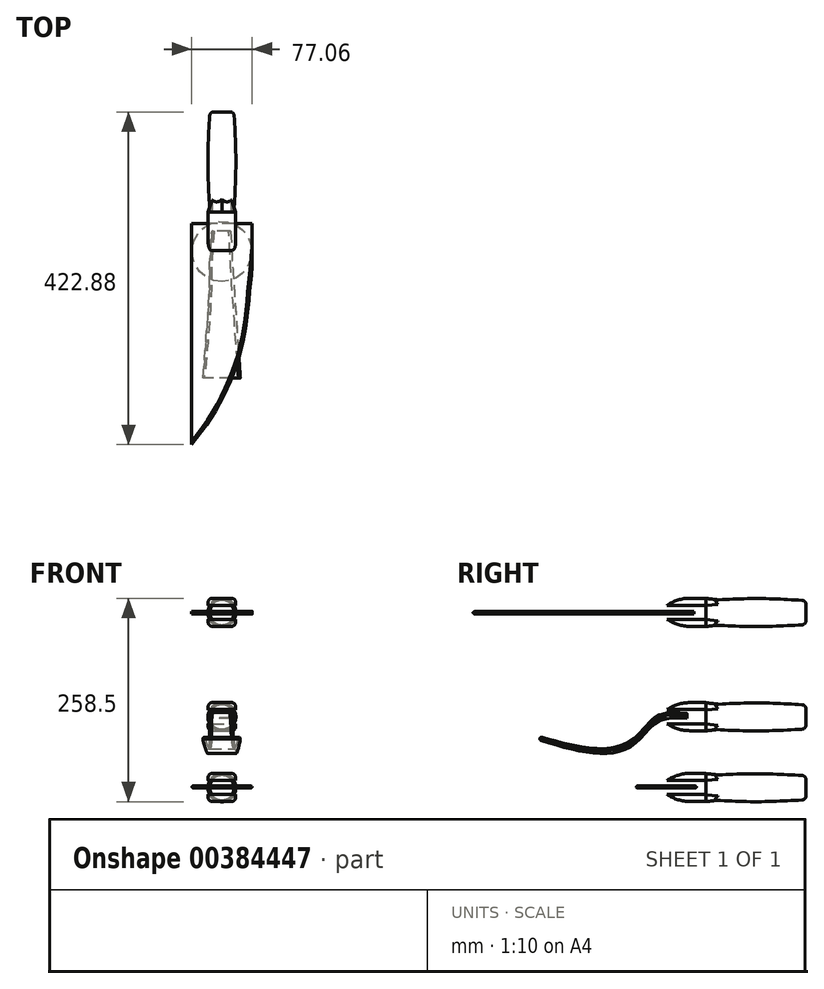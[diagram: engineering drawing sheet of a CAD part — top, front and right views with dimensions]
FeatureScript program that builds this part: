
annotation { "Feature Type Name" : "Feature", "Feature Type Description" : "" }
export const myFeature = defineFeature(function(context is Context, id is Id, definition is map)
    precondition{}
    {
        {
            var Q0;
            Q0=qCreatedBy(makeId("Front.planeOp"),FACE);
            cPlane(context, id + "F0", {"entities" : qUnion([Q0]), "cplaneType" : CPlaneType.OFFSET, "offset" : 63.5 * mm, "oppositeDirection" : true, "width" : 152.4 * mm, "height" : 152.4 * mm});
        }
        {
            var Q0;
            Q0=qCreatedBy(makeId("Front.planeOp"),FACE);
            cPlane(context, id + "F1", {"entities" : qUnion([Q0]), "cplaneType" : CPlaneType.OFFSET, "offset" : 63.5 * mm, "width" : 152.4 * mm, "height" : 152.4 * mm});
        }
        {
            var Q0;
            Q0=qCreatedBy(id+"F0.planeOp",FACE);
            var sketch = newSketch(context, id + "F2", { "sketchPlane" : qUnion([Q0])});
            skCircle(sketch, "E0", {"center": v(0, 0) * mm, "radius": 15.24 * mm});
            skSolve(sketch);
        }
        {
            var Q0;
            Q0=qCreatedBy(makeId("Front.planeOp"),FACE);
            var sketch = newSketch(context, id + "F3", { "sketchPlane" : qUnion([Q0])});
            skCircle(sketch, "E1", {"center": v(0, 0) * mm, "radius": 17.78 * mm});
            skSolve(sketch);
        }
        {
            var Q0;
            Q0=qCreatedBy(id+"F1.planeOp",FACE);
            var sketch = newSketch(context, id + "F4", { "sketchPlane" : qUnion([Q0])});
            skCircle(sketch, "E2", {"center": v(0, 0) * mm, "radius": 15.24 * mm});
            skSolve(sketch);
        }
        {
            var Q0;
            Q0=makeQuery(id+"F2.imprint","IMPRINT",FACE,{"disambiguationData":[TD([[makeQuery(id+"F2.imprint","IMPRINT",EDGE,{"derivedFrom":sQuery(id+"F2.wireOp",EDGE,"E0")}),1.0]])]});
            var Q1;
            Q1=makeQuery(id+"F3.imprint","IMPRINT",FACE,{"disambiguationData":[TD([[makeQuery(id+"F3.imprint","IMPRINT",EDGE,{"derivedFrom":sQuery(id+"F3.wireOp",EDGE,"E1")}),1.0]])]});
            var Q2;
            Q2=makeQuery(id+"F4.imprint","IMPRINT",FACE,{"disambiguationData":[TD([[makeQuery(id+"F4.imprint","IMPRINT",EDGE,{"derivedFrom":sQuery(id+"F4.wireOp",EDGE,"E2")}),1.0]])]});
            loft(context, id + "F5", {"sheetProfilesArray" : [{ "sheetProfileEntities" : qUnion([Q0]) }, { "sheetProfileEntities" : qUnion([Q1]) }, { "sheetProfileEntities" : qUnion([Q2]) }]});
        }
        {
            var Q0;
            Q0=makeQuery(id+"F5.opLoft","MID_CAP_EDGE",EDGE,{"disambiguationData":[OSD([sQuery(id+"F2.wireOp",EDGE,"E0")])],"capPos":0.0});
            fillet(context, id + "F6", {"entities" : qUnion([Q0]), "radius" : 5.08 * mm, "tangentPropagation" : true, "allowEdgeOverflow" : false});
        }
        {
            var Q0;
            Q0=qCreatedBy(id+"F1.planeOp",FACE);
            var sketch = newSketch(context, id + "F7", { "sketchPlane" : qUnion([Q0])});
            skLineSegment(sketch, "E3.bottom", {"start": v(-17.4, 18.02) * mm, "end": v(17.4, 18.02) * mm});
            skLineSegment(sketch, "E3.top", {"start": v(-17.4, 9.13) * mm, "end": v(17.4, 9.13) * mm});
            skLineSegment(sketch, "E3.left", {"start": v(-17.4, 18.02) * mm, "end": v(-17.4, 9.13) * mm});
            skLineSegment(sketch, "E3.right", {"start": v(17.4, 18.02) * mm, "end": v(17.4, 9.13) * mm});
            skPoint(sketch, "E3.middle", {"position": v(0, 13.57) * mm});
            skLineSegment(sketch, "E4.bottom", {"start": v(-17.4, -17.73) * mm, "end": v(17.4, -17.73) * mm});
            skLineSegment(sketch, "E4.top", {"start": v(-17.4, -8.84) * mm, "end": v(17.4, -8.84) * mm});
            skLineSegment(sketch, "E4.left", {"start": v(-17.4, -17.73) * mm, "end": v(-17.4, -8.84) * mm});
            skLineSegment(sketch, "E4.right", {"start": v(17.4, -17.73) * mm, "end": v(17.4, -8.84) * mm});
            skPoint(sketch, "E4.middle", {"position": v(0, -13.29) * mm});
            skSolve(sketch);
        }
        {
            var Q0;
            Q0=qCreatedBy(makeId("Front.planeOp"),FACE);
            cPlane(context, id + "F8", {"entities" : qUnion([Q0]), "cplaneType" : CPlaneType.OFFSET, "offset" : 45.97 * mm, "width" : 152.4 * mm, "height" : 152.4 * mm});
        }
        {
            var Q0;
            Q0=qCreatedBy(id+"F8.planeOp",FACE);
            var sketch = newSketch(context, id + "F9", { "sketchPlane" : qUnion([Q0])});
            skLineSegment(sketch, "E5.bottom", {"start": v(-11.43, 16.43) * mm, "end": v(11.43, 16.43) * mm});
            skLineSegment(sketch, "E5.top", {"start": v(-11.43, 10.72) * mm, "end": v(11.43, 10.72) * mm});
            skLineSegment(sketch, "E5.left", {"start": v(-11.43, 16.43) * mm, "end": v(-11.43, 10.72) * mm});
            skLineSegment(sketch, "E5.right", {"start": v(11.43, 16.43) * mm, "end": v(11.43, 10.72) * mm});
            skPoint(sketch, "E5.middle", {"position": v(0, 13.57) * mm});
            skLineSegment(sketch, "E6.bottom", {"start": v(-11.43, -15.95) * mm, "end": v(11.43, -15.95) * mm});
            skLineSegment(sketch, "E6.top", {"start": v(-11.43, -10.87) * mm, "end": v(11.43, -10.87) * mm});
            skLineSegment(sketch, "E6.left", {"start": v(-11.43, -15.95) * mm, "end": v(-11.43, -10.87) * mm});
            skLineSegment(sketch, "E6.right", {"start": v(11.43, -15.95) * mm, "end": v(11.43, -10.87) * mm});
            skPoint(sketch, "E6.middle", {"position": v(0, -13.4) * mm});
            skSolve(sketch);
        }
        {
            var Q0;
            Q0=qCreatedBy(id+"F8.planeOp",FACE);
            cPlane(context, id + "F10", {"entities" : qUnion([Q0]), "cplaneType" : CPlaneType.OFFSET, "offset" : 66.8 * mm, "width" : 152.4 * mm, "height" : 152.4 * mm});
        }
        {
            var Q0;
            Q0=qCreatedBy(id+"F10.planeOp",FACE);
            var sketch = newSketch(context, id + "F11", { "sketchPlane" : qUnion([Q0])});
            skLineSegment(sketch, "E7.bottom", {"start": v(-17.4, 18.22) * mm, "end": v(17.4, 18.22) * mm});
            skLineSegment(sketch, "E7.top", {"start": v(-17.4, 9.33) * mm, "end": v(17.4, 9.33) * mm});
            skLineSegment(sketch, "E7.left", {"start": v(-17.4, 18.22) * mm, "end": v(-17.4, 9.33) * mm});
            skLineSegment(sketch, "E7.right", {"start": v(17.4, 18.22) * mm, "end": v(17.4, 9.33) * mm});
            skPoint(sketch, "E7.middle", {"position": v(0, 13.77) * mm});
            skLineSegment(sketch, "E8.bottom", {"start": v(-17.4, -8.6) * mm, "end": v(17.4, -8.6) * mm});
            skLineSegment(sketch, "E8.top", {"start": v(-17.4, -17.49) * mm, "end": v(17.4, -17.49) * mm});
            skLineSegment(sketch, "E8.left", {"start": v(-17.4, -8.6) * mm, "end": v(-17.4, -17.49) * mm});
            skLineSegment(sketch, "E8.right", {"start": v(17.4, -8.6) * mm, "end": v(17.4, -17.49) * mm});
            skPoint(sketch, "E8.middle", {"position": v(0, -13.04) * mm});
            skSolve(sketch);
        }
        {
            var Q1;
            Q1=makeQuery(id+"F7.imprint","IMPRINT",FACE,{"disambiguationData":[TD([[makeQuery(id+"F7.imprint","IMPRINT",EDGE,{"derivedFrom":sQuery(id+"F7.wireOp",EDGE,"E3.bottom")}),-1.0]])]});
            var Q2;
            Q2=makeQuery(id+"F9.imprint","IMPRINT",FACE,{"disambiguationData":[TD([[makeQuery(id+"F9.imprint","IMPRINT",EDGE,{"derivedFrom":sQuery(id+"F9.wireOp",EDGE,"E5.bottom")}),-1.0]])]});
            loft(context, id + "F12", {"operationType" : NewBodyOperationType.ADD, "sheetProfilesArray" : [{ "sheetProfileEntities" : qUnion([Q1]) }, { "sheetProfileEntities" : qUnion([Q2]) }]});
        }
        {
            var Q1;
            Q1=makeQuery(id+"F7.imprint","IMPRINT",FACE,{"disambiguationData":[TD([[makeQuery(id+"F7.imprint","IMPRINT",EDGE,{"derivedFrom":sQuery(id+"F7.wireOp",EDGE,"E4.bottom")}),1.0]])]});
            var Q2;
            Q2=makeQuery(id+"F9.imprint","IMPRINT",FACE,{"disambiguationData":[TD([[makeQuery(id+"F9.imprint","IMPRINT",EDGE,{"derivedFrom":sQuery(id+"F9.wireOp",EDGE,"E6.bottom")}),1.0]])]});
            loft(context, id + "F13", {"operationType" : NewBodyOperationType.ADD, "sheetProfilesArray" : [{ "sheetProfileEntities" : qUnion([Q1]) }, { "sheetProfileEntities" : qUnion([Q2]) }]});
        }
        {
            var Q0;
            Q0=makeQuery(id+"F11.imprint","IMPRINT",FACE,{"disambiguationData":[TD([[makeQuery(id+"F11.imprint","IMPRINT",EDGE,{"derivedFrom":sQuery(id+"F11.wireOp",EDGE,"E7.bottom")}),-1.0]])]});
            extrude(context, id + "F14", {"entities" : qUnion([Q0]), "operationType" : NewBodyOperationType.ADD, "oppositeDirection" : true, "depth" : 49.28 * mm});
        }
        {
            var Q0;
            Q0=makeQuery(id+"F11.imprint","IMPRINT",FACE,{"disambiguationData":[TD([[makeQuery(id+"F11.imprint","IMPRINT",EDGE,{"derivedFrom":sQuery(id+"F11.wireOp",EDGE,"E8.bottom")}),-1.0]])]});
            extrude(context, id + "F15", {"entities" : qUnion([Q0]), "operationType" : NewBodyOperationType.ADD, "oppositeDirection" : true, "depth" : 49.53 * mm});
        }
        {
            var Q0;
            Q0=makeQuery(id+"F14.opExtrude","CAP_EDGE",EDGE,{"disambiguationData":[OSD([sQuery(id+"F11.wireOp",EDGE,"E7.bottom")])],"isStart":true});
            var Q1;
            Q1=makeQuery(id+"F15.opExtrude","CAP_EDGE",EDGE,{"disambiguationData":[OSD([sQuery(id+"F11.wireOp",EDGE,"E8.top")])],"isStart":true});
            fillet(context, id + "F16", {"entities" : qUnion([Q0, Q1]), "radius" : 50.8 * mm, "tangentPropagation" : true, "allowEdgeOverflow" : false});
        }
        {
            var Q0;
            Q0=makeQuery(id+"F13.opLoft","SWEPT_EDGE",EDGE,{"disambiguationData":[OSD([sQuery(id+"F7.wireOp",EDGE,"E4.bottom"),sQuery(id+"F7.wireOp",EDGE,"E4.left"),sQuery(id+"F9.wireOp",EDGE,"E6.bottom"),sQuery(id+"F9.wireOp",EDGE,"E6.left")])]});
            var Q1;
            Q1=makeQuery(id+"F13.opLoft","SWEPT_EDGE",EDGE,{"disambiguationData":[OSD([sQuery(id+"F7.wireOp",EDGE,"E4.bottom"),sQuery(id+"F7.wireOp",EDGE,"E4.right"),sQuery(id+"F9.wireOp",EDGE,"E6.bottom"),sQuery(id+"F9.wireOp",EDGE,"E6.right")])]});
            var Q2;
            Q2=makeQuery(id+"F12.opLoft","SWEPT_EDGE",EDGE,{"disambiguationData":[OSD([sQuery(id+"F7.wireOp",EDGE,"E3.bottom"),sQuery(id+"F7.wireOp",EDGE,"E3.left"),sQuery(id+"F9.wireOp",EDGE,"E5.bottom"),sQuery(id+"F9.wireOp",EDGE,"E5.left")])]});
            var Q3;
            Q3=makeQuery(id+"F12.opLoft","SWEPT_EDGE",EDGE,{"disambiguationData":[OSD([sQuery(id+"F7.wireOp",EDGE,"E3.bottom"),sQuery(id+"F7.wireOp",EDGE,"E3.right"),sQuery(id+"F9.wireOp",EDGE,"E5.bottom"),sQuery(id+"F9.wireOp",EDGE,"E5.right")])]});
            fillet(context, id + "F17", {"entities" : qUnion([Q0, Q1, Q2, Q3]), "radius" : 25.4 * mm, "tangentPropagation" : true, "allowEdgeOverflow" : false});
        }
        {
            var Q0;
            Q0=makeQuery(id+"F14.opExtrude","SWEPT_EDGE",EDGE,{"disambiguationData":[OSD([sQuery(id+"F11.wireOp",EDGE,"E7.bottom"),sQuery(id+"F11.wireOp",EDGE,"E7.right")])]});
            var Q1;
            Q1=makeQuery(id+"F14.opExtrude","SWEPT_EDGE",EDGE,{"disambiguationData":[OSD([sQuery(id+"F11.wireOp",EDGE,"E7.bottom"),sQuery(id+"F11.wireOp",EDGE,"E7.left")])]});
            var Q2;
            {var subQ3=sQuery(id+"F11.wireOp",EDGE,"E8.left");var subQ4=sQuery(id+"F11.wireOp",EDGE,"E8.top");Q2=makeQuery(id+"F15.boolean.opBoolean","SPLIT",EDGE,{"disambiguationData":[TD([makeQuery(id+"F15.opExtrude","CAP_FACE",FACE,{"disambiguationData":[OSD([sQuery(id+"F11.wireOp",EDGE,"E8.bottom"),subQ4,subQ3,sQuery(id+"F11.wireOp",EDGE,"E8.right")])],"isStart":false})])],"derivedFrom":makeQuery(id+"F15.opExtrude","SWEPT_EDGE",EDGE,{"disambiguationData":[OSD([subQ4,subQ3])]})});}
            var Q3;
            {var subQ3=sQuery(id+"F11.wireOp",EDGE,"E8.right");var subQ4=sQuery(id+"F11.wireOp",EDGE,"E8.top");Q3=makeQuery(id+"F15.boolean.opBoolean","SPLIT",EDGE,{"disambiguationData":[TD([makeQuery(id+"F15.opExtrude","CAP_FACE",FACE,{"disambiguationData":[OSD([sQuery(id+"F11.wireOp",EDGE,"E8.bottom"),subQ4,sQuery(id+"F11.wireOp",EDGE,"E8.left"),subQ3])],"isStart":false})])],"derivedFrom":makeQuery(id+"F15.opExtrude","SWEPT_EDGE",EDGE,{"disambiguationData":[OSD([subQ4,subQ3])]})});}
            fillet(context, id + "F18", {"entities" : qUnion([Q0, Q1, Q2, Q3]), "radius" : 5.08 * mm, "tangentPropagation" : true, "allowEdgeOverflow" : false});
        }
        {
            var Q0;
            Q0=qCreatedBy(makeId("Front.planeOp"),FACE);
            cPlane(context, id + "F19", {"entities" : qUnion([Q0]), "cplaneType" : CPlaneType.OFFSET, "offset" : 90.68 * mm, "width" : 152.4 * mm, "height" : 152.4 * mm});
        }
        {
            var Q0;
            Q0=qCreatedBy(id+"F19.planeOp",FACE);
            var sketch = newSketch(context, id + "F20", { "sketchPlane" : qUnion([Q0])});
            skLineSegment(sketch, "E9", {"start": v(28.47, 0) * mm, "end": v(-29.24, 0) * mm, "construction": true});
            skSolve(sketch);
        }
        {
            var Q0;
            Q0=sQuery(id+"F20.wireOp",EDGE,"E9");
            cPlane(context, id + "F21", {"entities" : qUnion([Q0]), "cplaneType" : CPlaneType.LINE_ANGLE, "offset" : 25.4 * mm, "angle" : 90 * degree, "width" : 152.4 * mm, "height" : 152.4 * mm});
        }
        {
            var Q0;
            Q0=qCreatedBy(id+"F21.planeOp",FACE);
            var sketch = newSketch(context, id + "F22", { "sketchPlane" : qUnion([Q0])});
            skCircle(sketch, "E10", {"center": v(0, -113.92) * mm, "radius": 38.1 * mm});
            skSolve(sketch);
        }
        {
            var Q0;
            Q0=makeQuery(id+"F22.imprint","IMPRINT",FACE,{"disambiguationData":[TD([[makeQuery(id+"F22.imprint","IMPRINT",EDGE,{"derivedFrom":sQuery(id+"F22.wireOp",EDGE,"E10")}),1.0]])]});
            extrude(context, id + "F23", {"entities" : qUnion([Q0]), "depth" : 2.03 * mm});
        }
        {
            var Q0;
            Q0=makeQuery(id+"F23.opExtrude","CAP_EDGE",EDGE,{"disambiguationData":[OSD([sQuery(id+"F22.wireOp",EDGE,"E10")])],"isStart":true});
            var Q1;
            Q1=makeQuery(id+"F23.opExtrude","CAP_EDGE",EDGE,{"disambiguationData":[OSD([sQuery(id+"F22.wireOp",EDGE,"E10")])],"isStart":false});
            fillet(context, id + "F24", {"entities" : qUnion([Q0, Q1]), "radius" : 1.02 * mm, "tangentPropagation" : true, "allowEdgeOverflow" : false});
        }
        {
            var Q0;
            Q0=makeQuery(id+"F5.opLoft","SWEPT_BODY",BODY,{"disambiguationData":[OSD([makeQuery(id+"F2.imprint","IMPRINT",FACE,{"disambiguationData":[TD([[makeQuery(id+"F2.imprint","IMPRINT",EDGE,{"derivedFrom":sQuery(id+"F2.wireOp",EDGE,"E0")}),1.0]])]}),sQuery(id+"F3.wireOp",EDGE,"E1"),makeQuery(id+"F4.imprint","IMPRINT",FACE,{"disambiguationData":[TD([[makeQuery(id+"F4.imprint","IMPRINT",EDGE,{"derivedFrom":sQuery(id+"F4.wireOp",EDGE,"E2")}),1.0]])]})])]});
            transform(context, id + "F25", {"entities" : qUnion([Q0]), "transformType" : TransformType.TRANSLATION_3D, "dx" : 0 * mm, "dy" : 0 * mm, "dz" : 89.92 * mm, "makeCopy" : true});
        }
        {
            var Q0;
            Q0=qCreatedBy(id+"F21.planeOp",FACE);
            cPlane(context, id + "F26", {"entities" : qUnion([Q0]), "cplaneType" : CPlaneType.OFFSET, "offset" : 91.7 * mm, "width" : 152.4 * mm, "height" : 152.4 * mm});
        }
        {
            var Q0;
            Q0=qCreatedBy(id+"F26.planeOp",FACE);
            var sketch = newSketch(context, id + "F27", { "sketchPlane" : qUnion([Q0])});
            skLineSegment(sketch, "E11", {"start": v(-24.98, -87.77) * mm, "end": v(24.86, -87.77) * mm, "construction": true});
            skSolve(sketch);
        }
        {
            var Q0;
            Q0=sQuery(id+"F27.wireOp",EDGE,"E11");
            cPlane(context, id + "F28", {"entities" : qUnion([Q0]), "cplaneType" : CPlaneType.LINE_ANGLE, "offset" : 25.4 * mm, "angle" : 0 * degree, "width" : 152.4 * mm, "height" : 152.4 * mm});
        }
        {
            var Q0;
            Q0=qCreatedBy(id+"F28.planeOp",FACE);
            var sketch = newSketch(context, id + "F29", { "sketchPlane" : qUnion([Q0])});
            skLineSegment(sketch, "E12.bottom", {"start": v(-11.27, 88.13) * mm, "end": v(12.68, 88.13) * mm});
            skLineSegment(sketch, "E12.top", {"start": v(-11.27, 94.6) * mm, "end": v(12.68, 94.6) * mm});
            skLineSegment(sketch, "E12.left", {"start": v(-11.27, 88.13) * mm, "end": v(-11.27, 94.6) * mm});
            skLineSegment(sketch, "E12.right", {"start": v(12.68, 88.13) * mm, "end": v(12.68, 94.6) * mm});
            skPoint(sketch, "E12.middle", {"position": v(0.7, 91.37) * mm});
            skSolve(sketch);
        }
        {
            var Q0;
            Q0=qCreatedBy(id+"F28.planeOp",FACE);
            cPlane(context, id + "F30", {"entities" : qUnion([Q0]), "cplaneType" : CPlaneType.OFFSET, "offset" : 37.85 * mm, "oppositeDirection" : true, "width" : 152.4 * mm, "height" : 152.4 * mm});
        }
        {
            var Q0;
            Q0=qCreatedBy(id+"F30.planeOp",FACE);
            var sketch = newSketch(context, id + "F31", { "sketchPlane" : qUnion([Q0])});
            skLineSegment(sketch, "E13.bottom", {"start": v(15.27, 90.72) * mm, "end": v(-13.2, 90.72) * mm});
            skLineSegment(sketch, "E13.top", {"start": v(15.27, 83.6) * mm, "end": v(-13.2, 83.6) * mm});
            skLineSegment(sketch, "E13.left", {"start": v(15.27, 90.72) * mm, "end": v(15.27, 83.6) * mm});
            skLineSegment(sketch, "E13.right", {"start": v(-13.2, 90.72) * mm, "end": v(-13.2, 83.6) * mm});
            skPoint(sketch, "E13.middle", {"position": v(1.03, 87.16) * mm});
            skSolve(sketch);
        }
        {
            var Q0;
            Q0=qCreatedBy(id+"F30.planeOp",FACE);
            cPlane(context, id + "F32", {"entities" : qUnion([Q0]), "cplaneType" : CPlaneType.OFFSET, "offset" : 24.9 * mm, "oppositeDirection" : true, "width" : 152.4 * mm, "height" : 152.4 * mm});
        }
        {
            var Q0;
            Q0=qCreatedBy(id+"F32.planeOp",FACE);
            var sketch = newSketch(context, id + "F33", { "sketchPlane" : qUnion([Q0])});
            skLineSegment(sketch, "E14.bottom", {"start": v(15.6, 66.13) * mm, "end": v(-14.82, 66.13) * mm});
            skLineSegment(sketch, "E14.top", {"start": v(15.6, 59) * mm, "end": v(-14.82, 59) * mm});
            skLineSegment(sketch, "E14.left", {"start": v(15.6, 66.13) * mm, "end": v(15.6, 59) * mm});
            skLineSegment(sketch, "E14.right", {"start": v(-14.82, 66.13) * mm, "end": v(-14.82, 59) * mm});
            skPoint(sketch, "E14.middle", {"position": v(0.38, 62.57) * mm});
            skSolve(sketch);
        }
        {
            var Q0;
            Q0=qCreatedBy(id+"F32.planeOp",FACE);
            cPlane(context, id + "F34", {"entities" : qUnion([Q0]), "cplaneType" : CPlaneType.OFFSET, "offset" : 124.2 * mm, "oppositeDirection" : true, "width" : 152.4 * mm, "height" : 152.4 * mm});
        }
        {
            var Q0;
            Q0=qCreatedBy(id+"F34.planeOp",FACE);
            var sketch = newSketch(context, id + "F35", { "sketchPlane" : qUnion([Q0])});
            skLineSegment(sketch, "E15.bottom", {"start": v(24.2, 60.76) * mm, "end": v(-23.4, 60.76) * mm});
            skLineSegment(sketch, "E15.top", {"start": v(24.2, 64.84) * mm, "end": v(-23.4, 64.84) * mm});
            skLineSegment(sketch, "E15.left", {"start": v(24.2, 60.76) * mm, "end": v(24.2, 64.84) * mm});
            skLineSegment(sketch, "E15.right", {"start": v(-23.4, 60.76) * mm, "end": v(-23.4, 64.84) * mm});
            skPoint(sketch, "E15.middle", {"position": v(0.4, 62.8) * mm});
            skSolve(sketch);
        }
        {
            var Q0;
            Q0=makeQuery(id+"F29.imprint","IMPRINT",FACE,{"disambiguationData":[TD([[makeQuery(id+"F29.imprint","IMPRINT",EDGE,{"derivedFrom":sQuery(id+"F29.wireOp",EDGE,"E12.bottom")}),1.0]])]});
            var Q1;
            Q1=makeQuery(id+"F31.imprint","IMPRINT",FACE,{"disambiguationData":[TD([[makeQuery(id+"F31.imprint","IMPRINT",EDGE,{"derivedFrom":sQuery(id+"F31.wireOp",EDGE,"E13.bottom")}),1.0]])]});
            var Q2;
            Q2=makeQuery(id+"F33.imprint","IMPRINT",FACE,{"disambiguationData":[TD([[makeQuery(id+"F33.imprint","IMPRINT",EDGE,{"derivedFrom":sQuery(id+"F33.wireOp",EDGE,"E14.bottom")}),1.0]])]});
            var Q3;
            Q3=makeQuery(id+"F35.imprint","IMPRINT",FACE,{"disambiguationData":[TD([[makeQuery(id+"F35.imprint","IMPRINT",EDGE,{"derivedFrom":sQuery(id+"F35.wireOp",EDGE,"E15.bottom")}),-1.0]])]});
            loft(context, id + "F36", {"sheetProfilesArray" : [{ "sheetProfileEntities" : qUnion([Q0]) }, { "sheetProfileEntities" : qUnion([Q1]) }, { "sheetProfileEntities" : qUnion([Q2]) }, { "sheetProfileEntities" : qUnion([Q3]) }]});
        }
        {
            var Q0;
            Q0=makeQuery(id+"F36.opLoft","MID_CAP_EDGE",EDGE,{"disambiguationData":[OSD([sQuery(id+"F35.wireOp",EDGE,"E15.top"),sQuery(id+"F35.wireOp",EDGE,"E15.left"),sQuery(id+"F35.wireOp",EDGE,"E15.right")])],"capPos":3.0});
            var Q1;
            Q1=makeQuery(id+"F36.opLoft","MID_CAP_EDGE",EDGE,{"disambiguationData":[OSD([sQuery(id+"F35.wireOp",EDGE,"E15.bottom"),sQuery(id+"F35.wireOp",EDGE,"E15.left"),sQuery(id+"F35.wireOp",EDGE,"E15.right")])],"capPos":3.0});
            var Q2;
            Q2=makeQuery(id+"F36.opLoft","SWEPT_EDGE",EDGE,{"disambiguationData":[OSD([sQuery(id+"F29.wireOp",EDGE,"E12.top"),sQuery(id+"F29.wireOp",EDGE,"E12.left"),sQuery(id+"F31.wireOp",EDGE,"E13.bottom"),sQuery(id+"F31.wireOp",EDGE,"E13.right")])]});
            var Q3;
            Q3=makeQuery(id+"F36.opLoft","SWEPT_EDGE",EDGE,{"disambiguationData":[OSD([sQuery(id+"F29.wireOp",EDGE,"E12.top"),sQuery(id+"F29.wireOp",EDGE,"E12.right"),sQuery(id+"F31.wireOp",EDGE,"E13.bottom"),sQuery(id+"F31.wireOp",EDGE,"E13.left")])]});
            fillet(context, id + "F37", {"entities" : qUnion([Q0, Q1, Q2, Q3]), "radius" : 2.54 * mm, "tangentPropagation" : true, "allowEdgeOverflow" : false});
        }
        {
            var Q0;
            Q0=makeQuery(id+"F25.opPattern","COPY",BODY,{"derivedFrom":makeQuery(id+"F5.opLoft","SWEPT_BODY",BODY,{"disambiguationData":[OSD([makeQuery(id+"F2.imprint","IMPRINT",FACE,{"disambiguationData":[TD([[makeQuery(id+"F2.imprint","IMPRINT",EDGE,{"derivedFrom":sQuery(id+"F2.wireOp",EDGE,"E0")}),1.0]])]}),sQuery(id+"F3.wireOp",EDGE,"E1"),makeQuery(id+"F4.imprint","IMPRINT",FACE,{"disambiguationData":[TD([[makeQuery(id+"F4.imprint","IMPRINT",EDGE,{"derivedFrom":sQuery(id+"F4.wireOp",EDGE,"E2")}),1.0]])]})])]}),"instanceName":"1"});
            transform(context, id + "F38", {"entities" : qUnion([Q0]), "transformType" : TransformType.TRANSLATION_3D, "dx" : 0 * mm, "dy" : 0 * mm, "dz" : 132.6 * mm, "makeCopy" : true});
        }
        {
            var Q0;
            Q0=qCreatedBy(id+"F26.planeOp",FACE);
            cPlane(context, id + "F39", {"entities" : qUnion([Q0]), "cplaneType" : CPlaneType.OFFSET, "offset" : 130.56 * mm, "width" : 152.4 * mm, "height" : 152.4 * mm});
        }
        {
            var Q0;
            Q0=qCreatedBy(id+"F39.planeOp",FACE);
            var sketch = newSketch(context, id + "F40", { "sketchPlane" : qUnion([Q0])});
            skLineSegment(sketch, "E16.bottom", {"start": v(38.42, -78.65) * mm, "end": v(-38.64, -78.65) * mm});
            skLineSegment(sketch, "E16.left", {"start": v(38.42, -78.65) * mm, "end": v(38.42, -134.4) * mm});
            skLineSegment(sketch, "E16.right", {"start": v(-38.64, -78.65) * mm, "end": v(-38.64, -359.57) * mm});
            skFitSpline(sketch, "E17", {"points": [v(38.42, -134.4) * mm, v(33.5, -183.59) * mm, v(23.12, -244.25) * mm, v(-9.13, -318.04) * mm, v(-38.64, -359.57) * mm], "startDerivative": vector(-20.97, -213.3) * mm, "endDerivative": vector(-127.7, -161.77) * mm});
            skSolve(sketch);
        }
        {
            var Q0;
            Q0=makeQuery(id+"F40.imprint","IMPRINT",FACE,{"disambiguationData":[TD([[makeQuery(id+"F40.imprint","IMPRINT",EDGE,{"derivedFrom":sQuery(id+"F40.wireOp",EDGE,"E16.bottom")}),1.0]])]});
            extrude(context, id + "F41", {"entities" : qUnion([Q0]), "endBound" : BoundingType.SYMMETRIC, "depth" : 3.56 * mm});
        }
        {
            var Q0;
            Q0=makeQuery(id+"F41.opExtrude","CAP_EDGE",EDGE,{"disambiguationData":[OSD([sQuery(id+"F40.wireOp",EDGE,"E17")])],"isStart":false});
            var Q1;
            Q1=makeQuery(id+"F41.opExtrude","CAP_EDGE",EDGE,{"disambiguationData":[OSD([sQuery(id+"F40.wireOp",EDGE,"E17")])],"isStart":true});
            fillet(context, id + "F42", {"entities" : qUnion([Q0, Q1]), "radius" : 2.54 * mm, "tangentPropagation" : true, "allowEdgeOverflow" : false});
        }
    });
